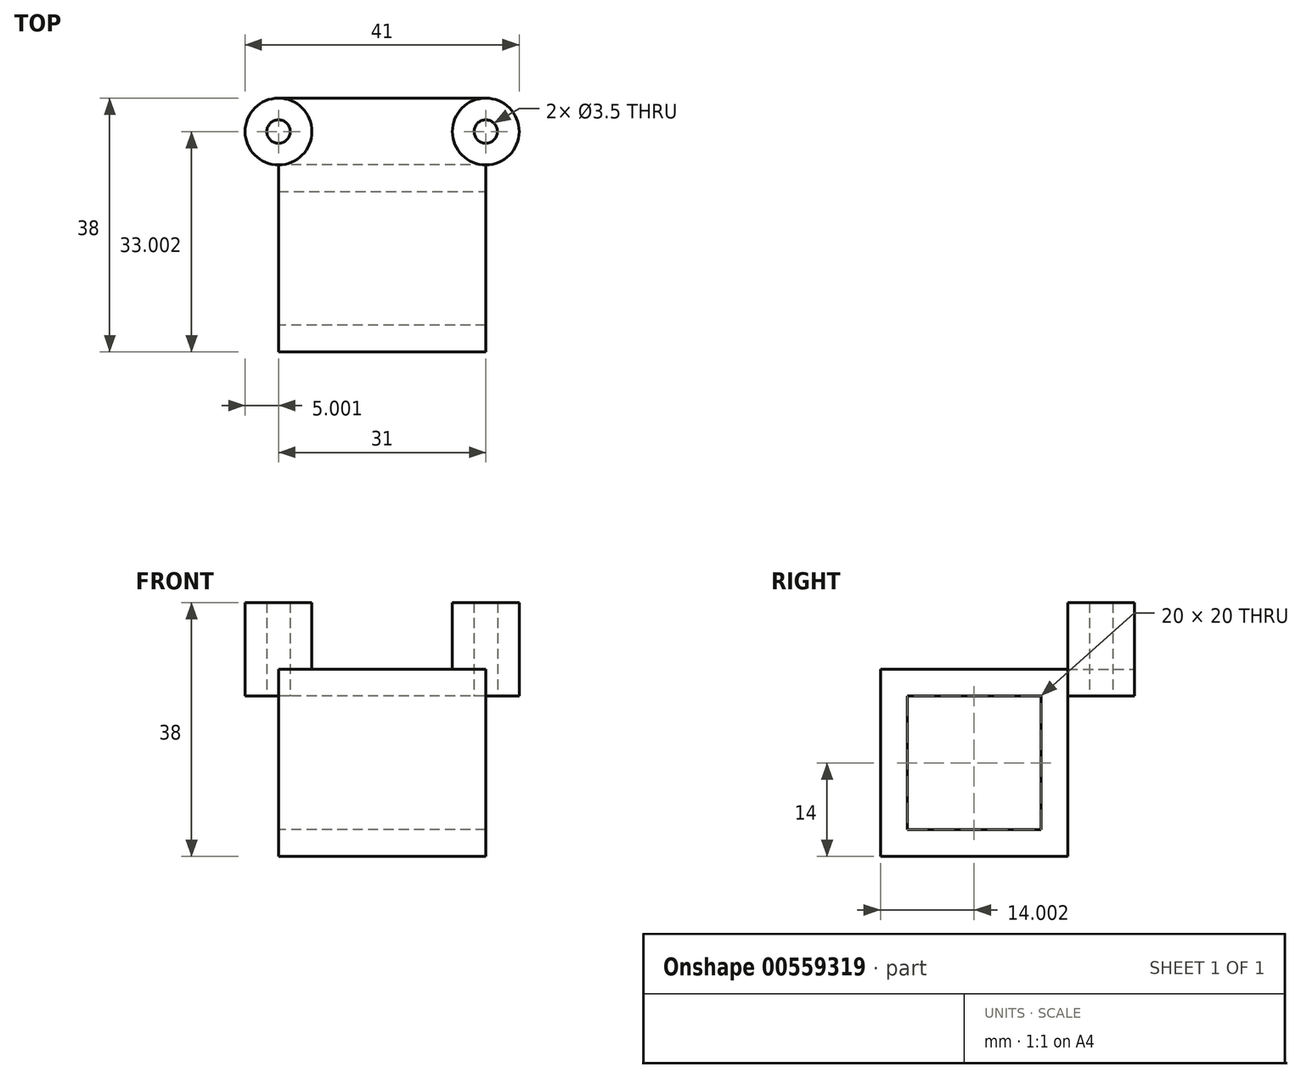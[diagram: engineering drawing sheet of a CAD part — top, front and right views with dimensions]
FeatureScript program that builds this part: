
annotation { "Feature Type Name" : "Feature", "Feature Type Description" : "" }
export const myFeature = defineFeature(function(context is Context, id is Id, definition is map)
    precondition{}
    {
        {
            var Q0;
            Q0=qCreatedBy(makeId("Top.planeOp"),FACE);
            var sketch = newSketch(context, id + "F0", { "sketchPlane" : qUnion([Q0])});
            skLineSegment(sketch, "E0", {"start": v(-4.15, -22.44) * mm, "end": v(26.85, -22.44) * mm});
            skCircle(sketch, "E1", {"center": v(26.85, -22.44) * mm, "radius": 1.75 * mm});
            skCircle(sketch, "E2", {"center": v(-4.15, -22.44) * mm, "radius": 1.75 * mm});
            skCircle(sketch, "E3", {"center": v(-4.15, -22.44) * mm, "radius": 5 * mm});
            skCircle(sketch, "E4", {"center": v(26.85, -22.44) * mm, "radius": 5 * mm});
            skLineSegment(sketch, "E5", {"start": v(-4.15, -22.44) * mm, "end": v(-4.15, -17.44) * mm, "construction": true});
            skLineSegment(sketch, "E6", {"start": v(-4.15, -17.44) * mm, "end": v(26.85, -17.44) * mm});
            skLineSegment(sketch, "E7", {"start": v(26.85, -17.44) * mm, "end": v(26.85, -27.44) * mm, "construction": true});
            skLineSegment(sketch, "E8", {"start": v(26.85, -27.44) * mm, "end": v(-4.15, -27.44) * mm});
            skLineSegment(sketch, "E9", {"start": v(-4.15, -27.44) * mm, "end": v(-4.15, -22.44) * mm, "construction": true});
            skSolve(sketch);
        }
        {
            var Q0;
            Q0=makeQuery(id+"F0.imprint","IMPRINT",FACE,{"disambiguationData":[TD([[makeQuery(id+"F0.imprint","IMPRINT",EDGE,{"derivedFrom":sQuery(id+"F0.wireOp",EDGE,"E2")}),-1.0]])]});
            var Q1;
            {var subQ5=sQuery(id+"F0.wireOp",EDGE,"E6");Q1=makeQuery(id+"F0.imprint","IMPRINT",FACE,{"disambiguationData":[TD([[makeQuery(id+"F0.imprint","IMPRINT",EDGE,{"derivedFrom":subQ5}),-1.0]])]});}
            var Q2;
            Q2=makeQuery(id+"F0.imprint","IMPRINT",FACE,{"disambiguationData":[TD([[makeQuery(id+"F0.imprint","IMPRINT",EDGE,{"derivedFrom":sQuery(id+"F0.wireOp",EDGE,"E1")}),-1.0]])]});
            var Q3;
            {var subQ5=sQuery(id+"F0.wireOp",EDGE,"E8");Q3=makeQuery(id+"F0.imprint","IMPRINT",FACE,{"disambiguationData":[TD([[makeQuery(id+"F0.imprint","IMPRINT",EDGE,{"derivedFrom":subQ5}),-1.0]])]});}
            extrude(context, id + "F1", {"entities" : qUnion([Q0, Q1, Q2, Q3]), "depth" : 4 * mm, "offsetDistance" : 25 * mm});
        }
        {
            var Q0;
            Q0=makeQuery(id+"F0.imprint","IMPRINT",FACE,{"disambiguationData":[TD([[makeQuery(id+"F0.imprint","IMPRINT",EDGE,{"derivedFrom":sQuery(id+"F0.wireOp",EDGE,"E2")}),-1.0]])]});
            var Q1;
            Q1=makeQuery(id+"F0.imprint","IMPRINT",FACE,{"disambiguationData":[TD([[makeQuery(id+"F0.imprint","IMPRINT",EDGE,{"derivedFrom":sQuery(id+"F0.wireOp",EDGE,"E1")}),-1.0]])]});
            extrude(context, id + "F2", {"entities" : qUnion([Q0, Q1]), "operationType" : NewBodyOperationType.ADD, "depth" : 14 * mm, "offsetDistance" : 25 * mm});
        }
        {
            var Q0;
            Q0=makeQuery(id+"F1.opExtrude","SWEPT_FACE",FACE,{"disambiguationData":[OSD([sQuery(id+"F0.wireOp",EDGE,"E8")])]});
            extrude(context, id + "F3", {"entities" : qUnion([Q0]), "operationType" : NewBodyOperationType.ADD, "depth" : 28 * mm, "offsetDistance" : 25 * mm});
        }
        {
            var Q0;
            {var subQ0=sQuery(id+"F0.wireOp",EDGE,"E8");Q0=makeQuery(id+"F3.boolean.opBoolean","MERGE",FACE,{"derivedFrom":[makeQuery(id+"F1.opExtrude","CAP_FACE",FACE,{"disambiguationData":[OSD([sQuery(id+"F0.wireOp",EDGE,"E1"),sQuery(id+"F0.wireOp",EDGE,"E2"),sQuery(id+"F0.wireOp",EDGE,"E3"),sQuery(id+"F0.wireOp",EDGE,"E4"),sQuery(id+"F0.wireOp",EDGE,"E6"),subQ0])],"isStart":true}),makeQuery(id+"F3.opExtrude","SWEPT_FACE",FACE,{"disambiguationData":[OSD([subQ0]),TDD([makeQuery(id+"F1.opExtrude","CAP_EDGE",EDGE,{"disambiguationData":[OSD([subQ0])],"isStart":true})])]})]});}
            var sketch = newSketch(context, id + "F4", { "sketchPlane" : qUnion([Q0])});
            skLineSegment(sketch, "E10", {"start": v(-4.15, 55.44) * mm, "end": v(26.85, 55.44) * mm});
            skLineSegment(sketch, "E11", {"start": v(26.85, 55.44) * mm, "end": v(26.85, 51.44) * mm});
            skLineSegment(sketch, "E12", {"start": v(26.85, 51.44) * mm, "end": v(-4.15, 51.44) * mm});
            skLineSegment(sketch, "E13", {"start": v(-4.15, 51.44) * mm, "end": v(-4.15, 55.44) * mm});
            skSolve(sketch);
        }
        {
            var Q0;
            Q0=makeQuery(id+"F4.imprint","IMPRINT",FACE,{"disambiguationData":[TD([[makeQuery(id+"F4.imprint","IMPRINT",EDGE,{"derivedFrom":sQuery(id+"F4.wireOp",EDGE,"E10")}),1.0]])]});
            extrude(context, id + "F5", {"entities" : qUnion([Q0]), "operationType" : NewBodyOperationType.ADD, "depth" : 24 * mm, "offsetDistance" : 25 * mm});
        }
        {
            var Q0;
            Q0=makeQuery(id+"F5.opExtrude","SWEPT_FACE",FACE,{"disambiguationData":[OSD([sQuery(id+"F4.wireOp",EDGE,"E12")])]});
            var sketch = newSketch(context, id + "F6", { "sketchPlane" : qUnion([Q0])});
            skLineSegment(sketch, "E14", {"start": v(-26.85, -24) * mm, "end": v(-26.85, -20) * mm});
            skLineSegment(sketch, "E15", {"start": v(-26.85, -20) * mm, "end": v(4.15, -20) * mm});
            skLineSegment(sketch, "E16", {"start": v(4.15, -20) * mm, "end": v(4.15, -24) * mm});
            skLineSegment(sketch, "E17", {"start": v(4.15, -24) * mm, "end": v(-26.85, -24) * mm});
            skSolve(sketch);
        }
        {
            var Q0;
            {var subQ0=sQuery(id+"F0.wireOp",EDGE,"E8");Q0=makeQuery(id+"F3.boolean.opBoolean","MERGE",FACE,{"derivedFrom":[makeQuery(id+"F1.opExtrude","CAP_FACE",FACE,{"disambiguationData":[OSD([sQuery(id+"F0.wireOp",EDGE,"E1"),sQuery(id+"F0.wireOp",EDGE,"E2"),sQuery(id+"F0.wireOp",EDGE,"E3"),sQuery(id+"F0.wireOp",EDGE,"E4"),sQuery(id+"F0.wireOp",EDGE,"E6"),subQ0])],"isStart":true}),makeQuery(id+"F3.opExtrude","SWEPT_FACE",FACE,{"disambiguationData":[OSD([subQ0]),TDD([makeQuery(id+"F1.opExtrude","CAP_EDGE",EDGE,{"disambiguationData":[OSD([subQ0])],"isStart":true})])]})]});}
            var sketch = newSketch(context, id + "F7", { "sketchPlane" : qUnion([Q0])});
            skLineSegment(sketch, "E18", {"start": v(26.85, 27.44) * mm, "end": v(-4.15, 27.44) * mm});
            skLineSegment(sketch, "E19", {"start": v(-4.15, 27.44) * mm, "end": v(-4.15, 31.44) * mm});
            skLineSegment(sketch, "E20", {"start": v(-4.15, 31.44) * mm, "end": v(26.85, 31.44) * mm});
            skLineSegment(sketch, "E21", {"start": v(26.85, 31.44) * mm, "end": v(26.85, 27.44) * mm});
            skSolve(sketch);
        }
        {
            var Q0;
            Q0=makeQuery(id+"F7.imprint","IMPRINT",FACE,{"disambiguationData":[TD([[makeQuery(id+"F7.imprint","IMPRINT",EDGE,{"derivedFrom":sQuery(id+"F7.wireOp",EDGE,"E18")}),-1.0]])]});
            extrude(context, id + "F8", {"entities" : qUnion([Q0]), "operationType" : NewBodyOperationType.ADD, "depth" : 24 * mm, "offsetDistance" : 25 * mm});
        }
        {
            var Q0;
            Q0=makeQuery(id+"F6.imprint","IMPRINT",FACE,{"disambiguationData":[TD([[makeQuery(id+"F6.imprint","IMPRINT",EDGE,{"derivedFrom":sQuery(id+"F6.wireOp",EDGE,"E14")}),-1.0]])]});
            extrude(context, id + "F9", {"entities" : qUnion([Q0]), "operationType" : NewBodyOperationType.ADD, "endBound" : BoundingType.UP_TO_NEXT, "depth" : 25 * mm, "offsetDistance" : 25 * mm});
        }
    });
